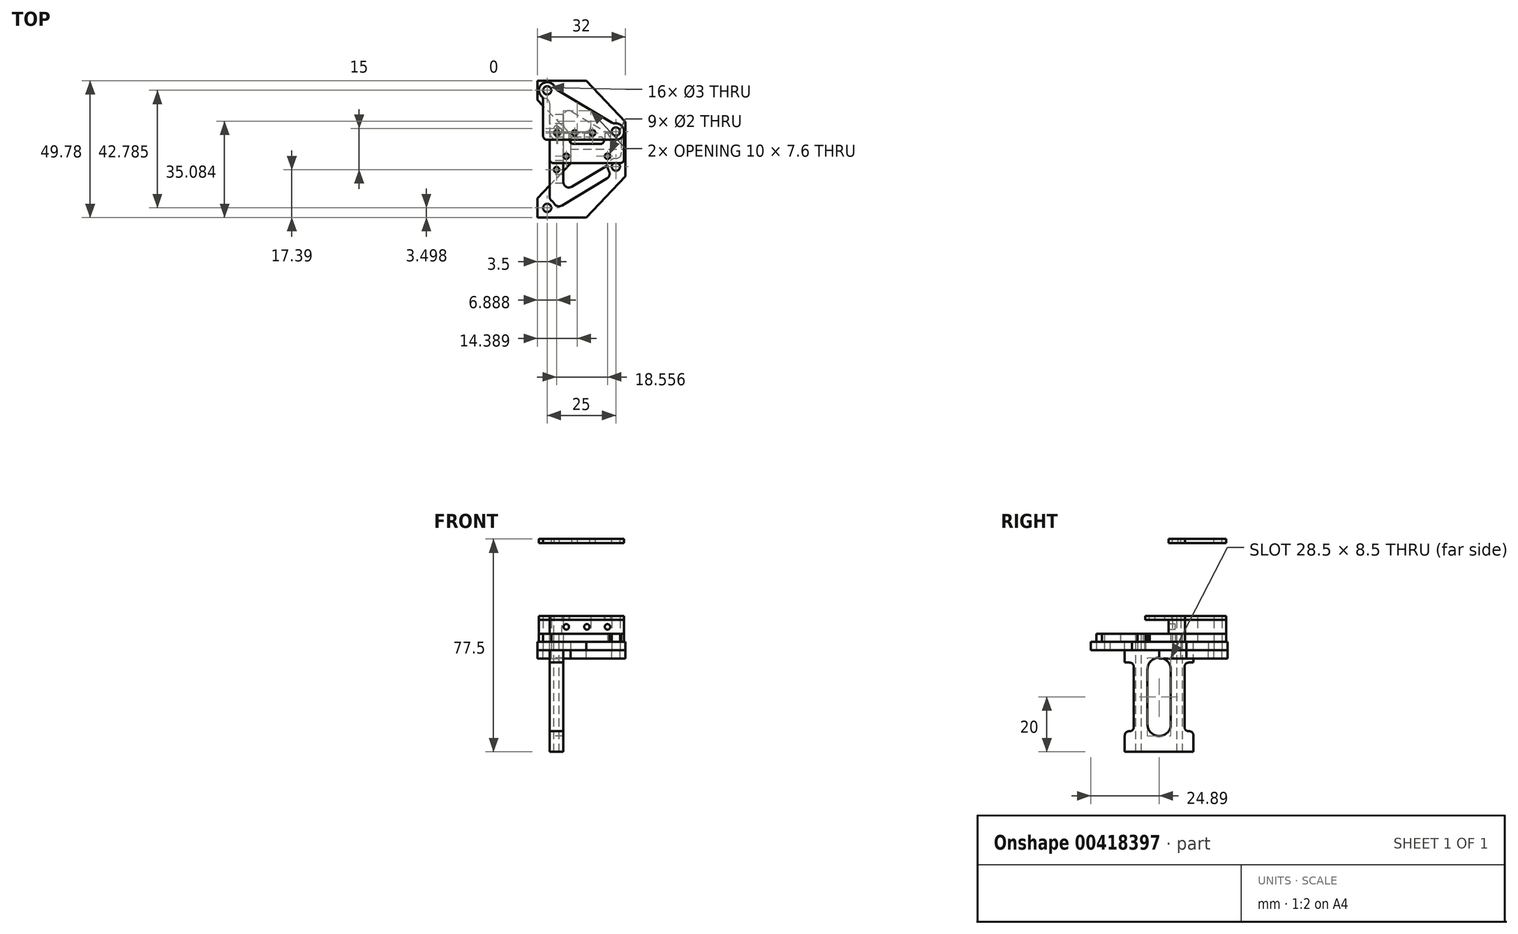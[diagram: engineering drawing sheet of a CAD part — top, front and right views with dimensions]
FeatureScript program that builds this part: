
annotation { "Feature Type Name" : "Feature", "Feature Type Description" : "" }
export const myFeature = defineFeature(function(context is Context, id is Id, definition is map)
    precondition{}
    {
        {
            var Q0;
            Q0=qCreatedBy(makeId("Top.planeOp"),FACE);
            var sketch = newSketch(context, id + "F0", { "sketchPlane" : qUnion([Q0])});
            skCircle(sketch, "E0", {"center": v(0, 21.4) * mm, "radius": 1.5 * mm});
            skCircle(sketch, "E1", {"center": v(25, 6.4) * mm, "radius": 1.5 * mm});
            skCircle(sketch, "E2.MirrorC", {"center": v(0, -21.4) * mm, "radius": 1.5 * mm});
            skCircle(sketch, "E3.MirrorC", {"center": v(25, -6.4) * mm, "radius": 1.5 * mm});
            skLineSegment(sketch, "E4", {"start": v(8.5, 5.26) * mm, "end": v(-3.5, 17.9) * mm});
            skLineSegment(sketch, "E5", {"start": v(-3.5, 17.9) * mm, "end": v(-3.5, 24.9) * mm});
            skLineSegment(sketch, "E6", {"start": v(-3.5, 24.9) * mm, "end": v(14.25, 24.9) * mm});
            skLineSegment(sketch, "E7", {"start": v(14.25, 24.9) * mm, "end": v(28.5, 9.9) * mm});
            skLineSegment(sketch, "E8", {"start": v(28.5, 9.9) * mm, "end": v(28.5, 0) * mm});
            skLineSegment(sketch, "E9.MirrorCS", {"start": v(8.5, -5.26) * mm, "end": v(-3.5, -17.9) * mm});
            skLineSegment(sketch, "E10.MirrorCS", {"start": v(-3.5, -17.9) * mm, "end": v(-3.5, -24.9) * mm});
            skLineSegment(sketch, "E11.MirrorCS", {"start": v(-3.5, -24.9) * mm, "end": v(14.25, -24.9) * mm});
            skLineSegment(sketch, "E12.MirrorCS", {"start": v(14.25, -24.9) * mm, "end": v(28.5, -9.9) * mm});
            skLineSegment(sketch, "E13.MirrorCS", {"start": v(28.5, -9.9) * mm, "end": v(28.5, 0) * mm});
            skLineSegment(sketch, "E14", {"start": v(8.5, 5.26) * mm, "end": v(8.5, -5.26) * mm});
            skPoint(sketch, "E15.orphan", {"position": v(13.5, 0) * mm});
            skLineSegment(sketch, "E16", {"start": v(8.5, 0) * mm, "end": v(28.5, 0) * mm});
            skSolve(sketch);
        }
        {
            var Q0;
            Q0=qSketchRegion(id+"F0",true);
            extrude(context, id + "F1", {"entities" : qUnion([Q0]), "depth" : 3 * mm, "offsetDistance" : 25 * mm});
        }
        {
            var Q0;
            Q0=makeQuery(id+"F0.imprint","IMPRINT",FACE,{"disambiguationData":[TD([[makeQuery(id+"F0.imprint","IMPRINT",EDGE,{"derivedFrom":sQuery(id+"F0.wireOp",EDGE,"E0")}),-1.0]])]});
            extrude(context, id + "F2", {"entities" : qUnion([Q0]), "oppositeDirection" : true, "depth" : 3 * mm, "offsetDistance" : 25 * mm});
        }
        {
            var Q0;
            Q0=makeQuery(id+"F1.opExtrude","CAP_FACE",FACE,{"disambiguationData":[OSD([sQuery(id+"F0.wireOp",EDGE,"E0"),sQuery(id+"F0.wireOp",EDGE,"E1"),sQuery(id+"F0.wireOp",EDGE,"E2.MirrorC"),sQuery(id+"F0.wireOp",EDGE,"E3.MirrorC"),sQuery(id+"F0.wireOp",EDGE,"E4"),sQuery(id+"F0.wireOp",EDGE,"E5"),sQuery(id+"F0.wireOp",EDGE,"E6"),sQuery(id+"F0.wireOp",EDGE,"E7"),sQuery(id+"F0.wireOp",EDGE,"E8"),sQuery(id+"F0.wireOp",EDGE,"E9.MirrorCS"),sQuery(id+"F0.wireOp",EDGE,"E10.MirrorCS"),sQuery(id+"F0.wireOp",EDGE,"E11.MirrorCS"),sQuery(id+"F0.wireOp",EDGE,"E12.MirrorCS"),sQuery(id+"F0.wireOp",EDGE,"E13.MirrorCS"),sQuery(id+"F0.wireOp",EDGE,"E14")])],"isStart":false});
            var sketch = newSketch(context, id + "F3", { "sketchPlane" : qUnion([Q0])});
            skCircle(sketch, "E17.0", {"center": v(0, 21.4) * mm, "radius": 1.5 * mm});
            skCircle(sketch, "E18.0", {"center": v(25, 6.4) * mm, "radius": 1.5 * mm});
            skCircle(sketch, "E19", {"center": v(0, 21.4) * mm, "radius": 3 * mm});
            skCircle(sketch, "E20", {"center": v(25, 6.4) * mm, "radius": 3 * mm});
            skPoint(sketch, "E21", {"position": v(1.5, 21.4) * mm});
            skPoint(sketch, "E22", {"position": v(3, 21.4) * mm});
            skPoint(sketch, "E23", {"position": v(26.5, 6.4) * mm});
            skPoint(sketch, "E24", {"position": v(28, 6.4) * mm});
            skLineSegment(sketch, "E25", {"start": v(0, 21.4) * mm, "end": v(25, 6.4) * mm, "construction": true});
            skCircle(sketch, "E26.0", {"center": v(25, -6.4) * mm, "radius": 1.5 * mm});
            skLineSegment(sketch, "E27", {"start": v(25, 6.4) * mm, "end": v(25, -6.4) * mm, "construction": true});
            skCircle(sketch, "E28.MirrorC", {"center": v(25, -6.4) * mm, "radius": 3 * mm});
            skCircle(sketch, "E29.MirrorC", {"center": v(0, -21.4) * mm, "radius": 3 * mm});
            skLineSegment(sketch, "E30", {"start": v(23, 4.16) * mm, "end": v(23, -4.16) * mm});
            skLineSegment(sketch, "E31.MirrorCS", {"start": v(27, 4.16) * mm, "end": v(27, -4.16) * mm});
            skLineSegment(sketch, "E32", {"start": v(0.89, 18.53) * mm, "end": v(22.05, 5.83) * mm});
            skLineSegment(sketch, "E33.MirrorCS", {"start": v(2.95, 21.96) * mm, "end": v(24.11, 9.26) * mm});
            skLineSegment(sketch, "E34.MirrorCS", {"start": v(0.89, -18.53) * mm, "end": v(22.05, -5.83) * mm});
            skLineSegment(sketch, "E35.MirrorCS", {"start": v(2.95, -21.96) * mm, "end": v(24.11, -9.26) * mm});
            skLineSegment(sketch, "E36", {"start": v(0.89, 18.53) * mm, "end": v(0.89, -18.53) * mm});
            skLineSegment(sketch, "E37", {"start": v(5.89, 15.53) * mm, "end": v(5.89, -15.53) * mm});
            skSolve(sketch);
        }
        {
            var Q0;
            Q0=makeQuery(id+"F3.imprint","IMPRINT",FACE,{"disambiguationData":[TD([[makeQuery(id+"F3.imprint","IMPRINT",EDGE,{"derivedFrom":sQuery(id+"F3.wireOp",EDGE,"E17.0")}),-1.0]])]});
            var Q1;
            Q1=makeQuery(id+"F3.imprint","IMPRINT",FACE,{"disambiguationData":[TD([[makeQuery(id+"F3.imprint","IMPRINT",EDGE,{"derivedFrom":makeQuery(id+"F1.opExtrude","CAP_EDGE",EDGE,{"disambiguationData":[OSD([sQuery(id+"F0.wireOp",EDGE,"E2.MirrorC")])],"isStart":false})}),1.0]])]});
            var Q2;
            {var subQ0=sQuery(id+"F3.wireOp",EDGE,"E30");Q2=makeQuery(id+"F3.imprint","IMPRINT",FACE,{"disambiguationData":[TD([[makeQuery(id+"F3.imprint","IMPRINT",EDGE,{"derivedFrom":subQ0}),1.0]])]});}
            var Q3;
            Q3=makeQuery(id+"F3.imprint","IMPRINT",FACE,{"disambiguationData":[TD([[makeQuery(id+"F3.imprint","IMPRINT",EDGE,{"derivedFrom":sQuery(id+"F3.wireOp",EDGE,"E18.0")}),-1.0]])]});
            var Q4;
            {var subQ6=sQuery(id+"F3.wireOp",EDGE,"E33.MirrorCS");Q4=makeQuery(id+"F3.imprint","IMPRINT",FACE,{"disambiguationData":[TD([[makeQuery(id+"F3.imprint","IMPRINT",EDGE,{"derivedFrom":subQ6}),-1.0]])]});}
            var Q5;
            Q5=makeQuery(id+"F3.imprint","IMPRINT",FACE,{"disambiguationData":[TD([[makeQuery(id+"F3.imprint","IMPRINT",EDGE,{"derivedFrom":sQuery(id+"F3.wireOp",EDGE,"E26.0")}),1.0]])]});
            var Q6;
            {var subQ6=sQuery(id+"F3.wireOp",EDGE,"E35.MirrorCS");Q6=makeQuery(id+"F3.imprint","IMPRINT",FACE,{"disambiguationData":[TD([[makeQuery(id+"F3.imprint","IMPRINT",EDGE,{"derivedFrom":subQ6}),1.0]])]});}
            var Q7;
            {var subQ1=sQuery(id+"F3.wireOp",EDGE,"E32");var subQ3=sQuery(id+"F3.wireOp",EDGE,"E37");var subQ4=makeQuery(id+"F3.imprint","INTERSECT",VERTEX,{"derivedFrom":[subQ1,subQ3]});Q7=makeQuery(id+"F3.imprint","IMPRINT",FACE,{"disambiguationData":[TD([[makeQuery(id+"F3.imprint","IMPRINT",EDGE,{"disambiguationData":[TD([[subQ4,-1.0]])],"derivedFrom":subQ3}),-1.0]])]});}
            var Q8;
            {var subQ1=sQuery(id+"F3.wireOp",EDGE,"E34.MirrorCS");var subQ3=sQuery(id+"F3.wireOp",EDGE,"E37");var subQ4=makeQuery(id+"F3.imprint","INTERSECT",VERTEX,{"derivedFrom":[subQ1,subQ3]});Q8=makeQuery(id+"F3.imprint","IMPRINT",FACE,{"disambiguationData":[TD([[makeQuery(id+"F3.imprint","IMPRINT",EDGE,{"disambiguationData":[TD([[subQ4,1.0]])],"derivedFrom":subQ3}),-1.0]])]});}
            var Q9;
            {var subQ0=sQuery(id+"F3.wireOp",EDGE,"E36");var subQ1=makeQuery(id+"F1.opExtrude","CAP_EDGE",EDGE,{"disambiguationData":[OSD([sQuery(id+"F0.wireOp",EDGE,"E4")])],"isStart":false});var subQ2=makeQuery(id+"F3.imprint","INTERSECT",VERTEX,{"derivedFrom":[subQ1,subQ0]});Q9=makeQuery(id+"F3.imprint","IMPRINT",FACE,{"disambiguationData":[TD([[makeQuery(id+"F3.imprint","IMPRINT",EDGE,{"disambiguationData":[TD([[subQ2,-1.0]])],"derivedFrom":subQ0}),1.0]])]});}
            extrude(context, id + "F4", {"entities" : qUnion([Q0, Q1, Q2, Q3, Q4, Q5, Q6, Q7, Q8, Q9]), "depth" : 3 * mm, "offsetDistance" : 25 * mm});
        }
        {
            var Q0;
            Q0=makeQuery(id+"F4.opExtrude","SWEPT_EDGE",EDGE,{"disambiguationData":[OSD([sQuery(id+"F3.wireOp",EDGE,"E19"),sQuery(id+"F3.wireOp",EDGE,"E32"),sQuery(id+"F3.wireOp",EDGE,"E36")])]});
            var Q1;
            Q1=makeQuery(id+"F4.opExtrude","SWEPT_EDGE",EDGE,{"disambiguationData":[OSD([sQuery(id+"F3.wireOp",EDGE,"E29.MirrorC"),sQuery(id+"F3.wireOp",EDGE,"E34.MirrorCS"),sQuery(id+"F3.wireOp",EDGE,"E36")])]});
            var Q2;
            Q2=makeQuery(id+"F4.opExtrude","SWEPT_EDGE",EDGE,{"disambiguationData":[OSD([sQuery(id+"F3.wireOp",EDGE,"E29.MirrorC"),sQuery(id+"F3.wireOp",EDGE,"E35.MirrorCS")])]});
            var Q3;
            Q3=makeQuery(id+"F4.opExtrude","SWEPT_EDGE",EDGE,{"disambiguationData":[OSD([sQuery(id+"F3.wireOp",EDGE,"E28.MirrorC"),sQuery(id+"F3.wireOp",EDGE,"E35.MirrorCS")])]});
            var Q4;
            Q4=makeQuery(id+"F4.opExtrude","SWEPT_EDGE",EDGE,{"disambiguationData":[OSD([sQuery(id+"F3.wireOp",EDGE,"E20"),sQuery(id+"F3.wireOp",EDGE,"E31.MirrorCS")])]});
            var Q5;
            Q5=makeQuery(id+"F4.opExtrude","SWEPT_EDGE",EDGE,{"disambiguationData":[OSD([sQuery(id+"F3.wireOp",EDGE,"E28.MirrorC"),sQuery(id+"F3.wireOp",EDGE,"E31.MirrorCS")])]});
            var Q6;
            Q6=makeQuery(id+"F4.opExtrude","SWEPT_EDGE",EDGE,{"disambiguationData":[OSD([sQuery(id+"F3.wireOp",EDGE,"E20"),sQuery(id+"F3.wireOp",EDGE,"E33.MirrorCS")])]});
            var Q7;
            Q7=makeQuery(id+"F4.opExtrude","SWEPT_EDGE",EDGE,{"disambiguationData":[OSD([sQuery(id+"F3.wireOp",EDGE,"E34.MirrorCS"),sQuery(id+"F3.wireOp",EDGE,"E37")])]});
            var Q8;
            Q8=makeQuery(id+"F4.opExtrude","SWEPT_EDGE",EDGE,{"disambiguationData":[OSD([sQuery(id+"F3.wireOp",EDGE,"E32"),sQuery(id+"F3.wireOp",EDGE,"E37")])]});
            var Q9;
            Q9=makeQuery(id+"F4.opExtrude","SWEPT_EDGE",EDGE,{"disambiguationData":[OSD([sQuery(id+"F3.wireOp",EDGE,"E19"),sQuery(id+"F3.wireOp",EDGE,"E33.MirrorCS")])]});
            fillet(context, id + "F5", {"entities" : qUnion([Q0, Q1, Q2, Q3, Q4, Q5, Q6, Q7, Q8, Q9]), "radius" : 2 * mm, "tangentPropagation" : true, "allowEdgeOverflow" : false});
        }
        {
            var Q0;
            Q0=makeQuery(id+"F4.opExtrude","CAP_FACE",FACE,{"disambiguationData":[OSD([sQuery(id+"F0.wireOp",EDGE,"E2.MirrorC"),sQuery(id+"F3.wireOp",EDGE,"E17.0"),sQuery(id+"F3.wireOp",EDGE,"E18.0"),sQuery(id+"F3.wireOp",EDGE,"E19"),sQuery(id+"F3.wireOp",EDGE,"E20"),sQuery(id+"F3.wireOp",EDGE,"E26.0"),sQuery(id+"F3.wireOp",EDGE,"E28.MirrorC"),sQuery(id+"F3.wireOp",EDGE,"E29.MirrorC"),sQuery(id+"F3.wireOp",EDGE,"E30"),sQuery(id+"F3.wireOp",EDGE,"E31.MirrorCS"),sQuery(id+"F3.wireOp",EDGE,"E32"),sQuery(id+"F3.wireOp",EDGE,"E33.MirrorCS"),sQuery(id+"F3.wireOp",EDGE,"E34.MirrorCS"),sQuery(id+"F3.wireOp",EDGE,"E35.MirrorCS"),sQuery(id+"F3.wireOp",EDGE,"E36"),sQuery(id+"F3.wireOp",EDGE,"E37")])],"isStart":false});
            var sketch = newSketch(context, id + "F6", { "sketchPlane" : qUnion([Q0])});
            skCircle(sketch, "E38.0", {"center": v(0, 21.4) * mm, "radius": 3 * mm});
            skCircle(sketch, "E39.0", {"center": v(0, 21.4) * mm, "radius": 1.5 * mm});
            skCircle(sketch, "E40.0", {"center": v(25, 6.4) * mm, "radius": 1.5 * mm});
            skCircle(sketch, "E41.0", {"center": v(25, 6.4) * mm, "radius": 3 * mm});
            skArc(sketch, "E42.0", {"start": v(3.6, 21.56) * mm, "mid": v(3.11, 21.98) * mm, "end": v(2.78, 22.52) * mm});
            skLineSegment(sketch, "E43.0", {"start": v(2.95, 21.96) * mm, "end": v(24.11, 9.26) * mm});
            skArc(sketch, "E44.0", {"start": v(24.7, 9.38) * mm, "mid": v(24.05, 9.41) * mm, "end": v(23.46, 9.65) * mm});
            skArc(sketch, "E45.0", {"start": v(-0.67, 18.47) * mm, "mid": v(0.45, 17.76) * mm, "end": v(0.89, 16.52) * mm});
            skLineSegment(sketch, "E46.0", {"start": v(0.89, 18.53) * mm, "end": v(0.89, 3.4) * mm});
            skArc(sketch, "E47.0", {"start": v(5.89, 12) * mm, "mid": v(6.9, 13.74) * mm, "end": v(8.92, 13.7) * mm});
            skLineSegment(sketch, "E48.0", {"start": v(5.89, 15.53) * mm, "end": v(5.89, 3.4) * mm});
            skLineSegment(sketch, "E49.0", {"start": v(0.89, 18.53) * mm, "end": v(14.92, 10.1) * mm});
            skLineSegment(sketch, "E50", {"start": v(25, 3.4) * mm, "end": v(5.89, 3.4) * mm});
            skLineSegment(sketch, "E51", {"start": v(5.89, 6.4) * mm, "end": v(13.9, 6.4) * mm});
            skLineSegment(sketch, "E52", {"start": v(5.89, 3.4) * mm, "end": v(0.89, 3.4) * mm});
            skPoint(sketch, "E53.orphan", {"position": v(0.89, -18.53) * mm});
            skPoint(sketch, "E54.orphan", {"position": v(5.89, -15.53) * mm});
            skPoint(sketch, "E55.newPointA", {"position": v(22.05, 5.83) * mm});
            skArc(sketch, "E55.filletArc", {"start": v(13.9, 6.4) * mm, "mid": v(15.82, 7.86) * mm, "end": v(14.92, 10.1) * mm});
            skSolve(sketch);
        }
        {
            var Q0;
            Q0=qSketchRegion(id+"F6",true);
            var Q1;
            {var subQ0=sQuery(id+"F6.wireOp",EDGE,"E47.0");Q1=makeQuery(id+"F6.imprint","IMPRINT",FACE,{"disambiguationData":[TD([[makeQuery(id+"F6.imprint","IMPRINT",EDGE,{"derivedFrom":subQ0}),1.0]])]});}
            extrude(context, id + "F7", {"entities" : qUnion([Q0, Q1]), "depth" : 5 * mm, "offsetDistance" : 25 * mm});
        }
        {
            var Q0;
            Q0=makeQuery(id+"F7.opExtrude","SWEPT_EDGE",EDGE,{"disambiguationData":[OSD([sQuery(id+"F6.wireOp",EDGE,"E48.0"),sQuery(id+"F6.wireOp",EDGE,"E51")])]});
            var Q1;
            Q1=makeQuery(id+"F7.opExtrude","SWEPT_EDGE",EDGE,{"disambiguationData":[OSD([sQuery(id+"F3.wireOp",EDGE,"E36"),sQuery(id+"F6.wireOp",EDGE,"E46.0"),sQuery(id+"F6.wireOp",EDGE,"E52")])]});
            fillet(context, id + "F8", {"entities" : qUnion([Q0, Q1]), "radius" : 3 * mm, "tangentPropagation" : true, "allowEdgeOverflow" : false});
        }
        {
            var Q0;
            Q0=makeQuery(id+"F4.opExtrude","CAP_FACE",FACE,{"disambiguationData":[OSD([sQuery(id+"F0.wireOp",EDGE,"E2.MirrorC"),sQuery(id+"F3.wireOp",EDGE,"E17.0"),sQuery(id+"F3.wireOp",EDGE,"E18.0"),sQuery(id+"F3.wireOp",EDGE,"E19"),sQuery(id+"F3.wireOp",EDGE,"E20"),sQuery(id+"F3.wireOp",EDGE,"E26.0"),sQuery(id+"F3.wireOp",EDGE,"E28.MirrorC"),sQuery(id+"F3.wireOp",EDGE,"E29.MirrorC"),sQuery(id+"F3.wireOp",EDGE,"E30"),sQuery(id+"F3.wireOp",EDGE,"E31.MirrorCS"),sQuery(id+"F3.wireOp",EDGE,"E32"),sQuery(id+"F3.wireOp",EDGE,"E33.MirrorCS"),sQuery(id+"F3.wireOp",EDGE,"E34.MirrorCS"),sQuery(id+"F3.wireOp",EDGE,"E35.MirrorCS"),sQuery(id+"F3.wireOp",EDGE,"E36"),sQuery(id+"F3.wireOp",EDGE,"E37")])],"isStart":false});
            var sketch = newSketch(context, id + "F9", { "sketchPlane" : qUnion([Q0])});
            skLineSegment(sketch, "E56", {"start": v(5.89, 0) * mm, "end": v(0.89, 0) * mm, "construction": true});
            skLineSegment(sketch, "E57", {"start": v(3.39, 0) * mm, "end": v(3.39, 16.52) * mm, "construction": true});
            skCircle(sketch, "E58", {"center": v(3.39, 7.5) * mm, "radius": 1 * mm});
            skCircle(sketch, "E59.MirrorC", {"center": v(3.39, -7.5) * mm, "radius": 1 * mm});
            skSolve(sketch);
        }
        {
            var Q0;
            Q0=qSketchRegion(id+"F9",true);
            extrude(context, id + "F10", {"entities" : qUnion([Q0]), "operationType" : NewBodyOperationType.REMOVE, "endBound" : BoundingType.UP_TO_NEXT, "oppositeDirection" : true, "depth" : 25 * mm, "offsetDistance" : 25 * mm});
        }
        {
            var Q0;
            Q0=makeQuery(id+"F7.opExtrude","CAP_FACE",FACE,{"disambiguationData":[OSD([sQuery(id+"F6.wireOp",EDGE,"E38.0"),sQuery(id+"F6.wireOp",EDGE,"E39.0"),sQuery(id+"F6.wireOp",EDGE,"E40.0"),sQuery(id+"F6.wireOp",EDGE,"E41.0"),sQuery(id+"F6.wireOp",EDGE,"E42.0"),sQuery(id+"F6.wireOp",EDGE,"E43.0"),sQuery(id+"F6.wireOp",EDGE,"E44.0"),sQuery(id+"F6.wireOp",EDGE,"E45.0"),sQuery(id+"F6.wireOp",EDGE,"E46.0"),sQuery(id+"F6.wireOp",EDGE,"E47.0"),sQuery(id+"F6.wireOp",EDGE,"E48.0"),sQuery(id+"F6.wireOp",EDGE,"E49.0"),sQuery(id+"F6.wireOp",EDGE,"E50"),sQuery(id+"F6.wireOp",EDGE,"E51"),sQuery(id+"F6.wireOp",EDGE,"E52"),sQuery(id+"F6.wireOp",EDGE,"E55.filletArc")])],"isStart":false});
            var sketch = newSketch(context, id + "F11", { "sketchPlane" : qUnion([Q0])});
            skArc(sketch, "E60.0", {"start": v(0.89, 6.4) * mm, "mid": v(1.77, 4.27) * mm, "end": v(3.89, 3.4) * mm, "construction": true});
            skCircle(sketch, "E61", {"center": v(3.89, 6.4) * mm, "radius": 1.5 * mm});
            skSolve(sketch);
        }
        {
            var Q0;
            Q0=qSketchRegion(id+"F11",true);
            extrude(context, id + "F12", {"entities" : qUnion([Q0]), "operationType" : NewBodyOperationType.REMOVE, "endBound" : BoundingType.UP_TO_NEXT, "oppositeDirection" : true, "depth" : 25 * mm, "offsetDistance" : 25 * mm});
        }
        {
            var Q0;
            Q0=makeQuery(id+"F7.opExtrude","SWEPT_FACE",FACE,{"disambiguationData":[OSD([sQuery(id+"F6.wireOp",EDGE,"E50"),sQuery(id+"F6.wireOp",EDGE,"E52")])]});
            var sketch = newSketch(context, id + "F13", { "sketchPlane" : qUnion([Q0])});
            skLineSegment(sketch, "E62", {"start": v(3.89, 8.5) * mm, "end": v(25, 8.5) * mm, "construction": true});
            skLineSegment(sketch, "E63", {"start": v(14.44, 11) * mm, "end": v(14.44, 6) * mm, "construction": true});
            skCircle(sketch, "E64", {"center": v(6.94, 8.5) * mm, "radius": 1 * mm});
            skCircle(sketch, "E65", {"center": v(14.44, 8.5) * mm, "radius": 1 * mm});
            skCircle(sketch, "E66.MirrorC", {"center": v(21.94, 8.5) * mm, "radius": 1 * mm});
            skSolve(sketch);
        }
        {
            var Q0;
            Q0 = qSketchRegion(id + "F13", true);
            extrude(context, id + "F14", {"entities" : qUnion([Q0]), "operationType" : NewBodyOperationType.REMOVE, "oppositeDirection" : true, "depth" : 2.5 * mm, "offsetDistance" : 25 * mm});
        }
        {
            var Q0;
            Q0=makeQuery(id+"F4.opExtrude","CAP_FACE",FACE,{"disambiguationData":[OSD([sQuery(id+"F0.wireOp",EDGE,"E2.MirrorC"),sQuery(id+"F3.wireOp",EDGE,"E17.0"),sQuery(id+"F3.wireOp",EDGE,"E18.0"),sQuery(id+"F3.wireOp",EDGE,"E19"),sQuery(id+"F3.wireOp",EDGE,"E20"),sQuery(id+"F3.wireOp",EDGE,"E26.0"),sQuery(id+"F3.wireOp",EDGE,"E28.MirrorC"),sQuery(id+"F3.wireOp",EDGE,"E29.MirrorC"),sQuery(id+"F3.wireOp",EDGE,"E30"),sQuery(id+"F3.wireOp",EDGE,"E31.MirrorCS"),sQuery(id+"F3.wireOp",EDGE,"E32"),sQuery(id+"F3.wireOp",EDGE,"E33.MirrorCS"),sQuery(id+"F3.wireOp",EDGE,"E34.MirrorCS"),sQuery(id+"F3.wireOp",EDGE,"E35.MirrorCS"),sQuery(id+"F3.wireOp",EDGE,"E36"),sQuery(id+"F3.wireOp",EDGE,"E37")])],"isStart":true});
            var sketch = newSketch(context, id + "F15", { "sketchPlane" : qUnion([Q0])});
            skCircle(sketch, "E67.0", {"center": v(3.39, 7.5) * mm, "radius": 1 * mm});
            skCircle(sketch, "E68.0", {"center": v(3.39, -7.5) * mm, "radius": 1 * mm});
            skLineSegment(sketch, "E69", {"start": v(3.39, 7.5) * mm, "end": v(3.39, -7.5) * mm, "construction": true});
            skLineSegment(sketch, "E70.bottom", {"start": v(0.89, 12.5) * mm, "end": v(5.89, 12.5) * mm});
            skLineSegment(sketch, "E70.top", {"start": v(0.89, -12.5) * mm, "end": v(5.89, -12.5) * mm});
            skLineSegment(sketch, "E70.left", {"start": v(0.89, 12.5) * mm, "end": v(0.89, -12.5) * mm});
            skLineSegment(sketch, "E70.right", {"start": v(5.89, 12.5) * mm, "end": v(5.89, -12.5) * mm});
            skPoint(sketch, "E70.middle", {"position": v(3.39, 0) * mm});
            skSolve(sketch);
        }
        {
            var Q0;
            Q0 = qSketchRegion(id + "F15", true);
            extrude(context, id + "F16", {"entities" : qUnion([Q0]), "depth" : 40 * mm, "offsetDistance" : 25 * mm});
        }
        {
            var Q0;
            Q0=makeQuery(id+"F16.opExtrude","SWEPT_FACE",FACE,{"disambiguationData":[OSD([sQuery(id+"F15.wireOp",EDGE,"E70.left")])]});
            var sketch = newSketch(context, id + "F17", { "sketchPlane" : qUnion([Q0])});
            skArc(sketch, "E71", {"start": v(4.25, -7) * mm, "mid": v(0, -2.75) * mm, "end": v(-4.25, -7) * mm});
            skLineSegment(sketch, "E72", {"start": v(0, 3) * mm, "end": v(0, -37) * mm, "construction": true});
            skLineSegment(sketch, "E73", {"start": v(12.5, -17) * mm, "end": v(-12.5, -17) * mm, "construction": true});
            skArc(sketch, "E74.MirrorC", {"start": v(4.25, -27) * mm, "mid": v(0, -31.25) * mm, "end": v(-4.25, -27) * mm});
            skLineSegment(sketch, "E75", {"start": v(4.25, -7) * mm, "end": v(4.25, -27) * mm});
            skLineSegment(sketch, "E76.MirrorCS", {"start": v(-4.25, -7) * mm, "end": v(-4.25, -27) * mm});
            skLineSegment(sketch, "E77.bottom", {"start": v(12.5, -4.5) * mm, "end": v(10.75, -4.5) * mm});
            skLineSegment(sketch, "E77.top", {"start": v(12.5, -29.5) * mm, "end": v(10.75, -29.5) * mm});
            skLineSegment(sketch, "E77.left", {"start": v(12.5, -4.5) * mm, "end": v(12.5, -29.5) * mm});
            skLineSegment(sketch, "E77.right", {"start": v(9.25, -6) * mm, "end": v(9.25, -28) * mm});
            skPoint(sketch, "E78", {"position": v(9.25, -17) * mm});
            skPoint(sketch, "E79.visualSharp", {"position": v(9.25, -4.5) * mm});
            skArc(sketch, "E79.filletArc", {"start": v(10.75, -4.5) * mm, "mid": v(9.69, -4.94) * mm, "end": v(9.25, -6) * mm});
            skPoint(sketch, "E80.visualSharp", {"position": v(9.25, -29.5) * mm});
            skArc(sketch, "E80.filletArc", {"start": v(9.25, -28) * mm, "mid": v(9.69, -29.06) * mm, "end": v(10.75, -29.5) * mm});
            skLineSegment(sketch, "E81.MirrorCS", {"start": v(-12.5, -29.5) * mm, "end": v(-10.75, -29.5) * mm});
            skLineSegment(sketch, "E82.MirrorCS", {"start": v(-12.5, -4.5) * mm, "end": v(-10.75, -4.5) * mm});
            skArc(sketch, "E83.MirrorCS", {"start": v(-9.25, -28) * mm, "mid": v(-9.69, -29.06) * mm, "end": v(-10.75, -29.5) * mm});
            skArc(sketch, "E84.MirrorCS", {"start": v(-10.75, -4.5) * mm, "mid": v(-9.69, -4.94) * mm, "end": v(-9.25, -6) * mm});
            skLineSegment(sketch, "E85.MirrorCS", {"start": v(-9.25, -6) * mm, "end": v(-9.25, -28) * mm});
            skPoint(sketch, "E86.MirrorP", {"position": v(-9.25, -29.5) * mm});
            skLineSegment(sketch, "E87.MirrorCS", {"start": v(-12.5, -4.5) * mm, "end": v(-12.5, -29.5) * mm});
            skPoint(sketch, "E88.MirrorP", {"position": v(-9.25, -4.5) * mm});
            skPoint(sketch, "E89.MirrorP", {"position": v(-9.25, -17) * mm});
            skSolve(sketch);
        }
        {
            var Q0;
            Q0 = qSketchRegion(id + "F17", true);
            extrude(context, id + "F18", {"entities" : qUnion([Q0]), "operationType" : NewBodyOperationType.REMOVE, "endBound" : BoundingType.UP_TO_NEXT, "oppositeDirection" : true, "depth" : 25 * mm, "offsetDistance" : 25 * mm});
        }
        {
            var Q0;
            Q0=makeQuery(id+"F18.boolean.opBoolean","COPY",EDGE,{"derivedFrom":makeQuery(id+"F18.opExtrude","SWEPT_EDGE",EDGE,{"disambiguationData":[OSD([sQuery(id+"F3.wireOp",EDGE,"E36"),sQuery(id+"F15.wireOp",EDGE,"E70.bottom"),sQuery(id+"F15.wireOp",EDGE,"E70.left"),sQuery(id+"F17.wireOp",EDGE,"E77.bottom"),sQuery(id+"F17.wireOp",EDGE,"E77.left")])]})});
            var Q1;
            Q1=makeQuery(id+"F18.boolean.opBoolean","COPY",EDGE,{"derivedFrom":makeQuery(id+"F18.opExtrude","SWEPT_EDGE",EDGE,{"disambiguationData":[OSD([sQuery(id+"F3.wireOp",EDGE,"E36"),sQuery(id+"F15.wireOp",EDGE,"E70.top"),sQuery(id+"F15.wireOp",EDGE,"E70.left"),sQuery(id+"F17.wireOp",EDGE,"E82.MirrorCS"),sQuery(id+"F17.wireOp",EDGE,"E87.MirrorCS")])]})});
            var Q2;
            Q2=makeQuery(id+"F18.boolean.opBoolean","COPY",EDGE,{"derivedFrom":makeQuery(id+"F18.opExtrude","SWEPT_EDGE",EDGE,{"disambiguationData":[OSD([sQuery(id+"F3.wireOp",EDGE,"E36"),sQuery(id+"F15.wireOp",EDGE,"E70.bottom"),sQuery(id+"F15.wireOp",EDGE,"E70.left"),sQuery(id+"F17.wireOp",EDGE,"E77.top"),sQuery(id+"F17.wireOp",EDGE,"E77.left")])]})});
            var Q3;
            Q3=makeQuery(id+"F18.boolean.opBoolean","COPY",EDGE,{"derivedFrom":makeQuery(id+"F18.opExtrude","SWEPT_EDGE",EDGE,{"disambiguationData":[OSD([sQuery(id+"F3.wireOp",EDGE,"E36"),sQuery(id+"F15.wireOp",EDGE,"E70.top"),sQuery(id+"F15.wireOp",EDGE,"E70.left"),sQuery(id+"F17.wireOp",EDGE,"E81.MirrorCS"),sQuery(id+"F17.wireOp",EDGE,"E87.MirrorCS")])]})});
            fillet(context, id + "F19", {"entities" : qUnion([Q0, Q1, Q2, Q3]), "radius" : 1.5 * mm, "tangentPropagation" : true, "allowEdgeOverflow" : false});
        }
        {
            var Q0;
            Q0=makeQuery(id+"F7.opExtrude","CAP_FACE",FACE,{"disambiguationData":[OSD([sQuery(id+"F6.wireOp",EDGE,"E38.0"),sQuery(id+"F6.wireOp",EDGE,"E39.0"),sQuery(id+"F6.wireOp",EDGE,"E40.0"),sQuery(id+"F6.wireOp",EDGE,"E41.0"),sQuery(id+"F6.wireOp",EDGE,"E42.0"),sQuery(id+"F6.wireOp",EDGE,"E43.0"),sQuery(id+"F6.wireOp",EDGE,"E44.0"),sQuery(id+"F6.wireOp",EDGE,"E45.0"),sQuery(id+"F6.wireOp",EDGE,"E46.0"),sQuery(id+"F6.wireOp",EDGE,"E47.0"),sQuery(id+"F6.wireOp",EDGE,"E48.0"),sQuery(id+"F6.wireOp",EDGE,"E49.0"),sQuery(id+"F6.wireOp",EDGE,"E50"),sQuery(id+"F6.wireOp",EDGE,"E51"),sQuery(id+"F6.wireOp",EDGE,"E52"),sQuery(id+"F6.wireOp",EDGE,"E55.filletArc")])],"isStart":false});
            var sketch = newSketch(context, id + "F20", { "sketchPlane" : qUnion([Q0])});
            skLineSegment(sketch, "E90.0.0", {"start": v(0.89, 16.52) * mm, "end": v(0.89, 6.4) * mm});
            skArc(sketch, "E90.0.3", {"start": v(28, 6.4) * mm, "mid": v(27, 8.62) * mm, "end": v(24.7, 9.38) * mm});
            skArc(sketch, "E90.0.4", {"start": v(24.7, 9.38) * mm, "mid": v(24.05, 9.41) * mm, "end": v(23.46, 9.65) * mm});
            skLineSegment(sketch, "E90.0.5", {"start": v(23.46, 9.65) * mm, "end": v(3.6, 21.56) * mm});
            skArc(sketch, "E90.0.6", {"start": v(3.6, 21.56) * mm, "mid": v(3.11, 21.98) * mm, "end": v(2.78, 22.52) * mm});
            skArc(sketch, "E90.0.7", {"start": v(2.78, 22.52) * mm, "mid": v(-2.29, 23.33) * mm, "end": v(-0.67, 18.47) * mm});
            skArc(sketch, "E90.0.8", {"start": v(-0.67, 18.47) * mm, "mid": v(0.45, 17.76) * mm, "end": v(0.89, 16.52) * mm});
            skArc(sketch, "E91.0", {"start": v(5.89, 12) * mm, "mid": v(6.9, 13.74) * mm, "end": v(8.92, 13.7) * mm});
            skLineSegment(sketch, "E92.0", {"start": v(8.92, 13.7) * mm, "end": v(14.92, 10.1) * mm});
            skLineSegment(sketch, "E93.0", {"start": v(5.89, 12) * mm, "end": v(5.89, 9.4) * mm});
            skArc(sketch, "E94.0", {"start": v(8.89, 6.4) * mm, "mid": v(6.77, 7.27) * mm, "end": v(5.89, 9.4) * mm});
            skLineSegment(sketch, "E95.0", {"start": v(8.89, 6.4) * mm, "end": v(13.9, 6.4) * mm});
            skArc(sketch, "E96.0", {"start": v(13.9, 6.4) * mm, "mid": v(15.82, 7.86) * mm, "end": v(14.92, 10.1) * mm});
            skCircle(sketch, "E97.0", {"center": v(25, 6.4) * mm, "radius": 1.5 * mm});
            skCircle(sketch, "E98.0", {"center": v(3.89, 6.4) * mm, "radius": 1.5 * mm});
            skCircle(sketch, "E99.0", {"center": v(0, 21.4) * mm, "radius": 1.5 * mm});
            skPoint(sketch, "E100", {"position": v(28, 6.4) * mm});
            skPoint(sketch, "E101.orphan", {"position": v(25, 3.4) * mm});
            skLineSegment(sketch, "E102", {"start": v(0.89, 6.4) * mm, "end": v(0.89, -3.6) * mm});
            skLineSegment(sketch, "E103", {"start": v(2.39, -5.1) * mm, "end": v(26.5, -5.1) * mm});
            skLineSegment(sketch, "E104", {"start": v(28, -3.6) * mm, "end": v(28, 6.4) * mm});
            skLineSegment(sketch, "E105", {"start": v(0.89, 3.14) * mm, "end": v(28, 3.14) * mm, "construction": true});
            skLineSegment(sketch, "E106", {"start": v(0.89, 3.4) * mm, "end": v(28, 3.4) * mm, "construction": true});
            skPoint(sketch, "E107.visualSharp", {"position": v(0.89, -5.1) * mm});
            skArc(sketch, "E107.filletArc", {"start": v(0.89, -3.6) * mm, "mid": v(1.33, -4.67) * mm, "end": v(2.39, -5.1) * mm});
            skPoint(sketch, "E108.visualSharp", {"position": v(28, -5.1) * mm});
            skArc(sketch, "E108.filletArc", {"start": v(26.5, -5.1) * mm, "mid": v(27.56, -4.67) * mm, "end": v(28, -3.6) * mm});
            skPoint(sketch, "E109", {"position": v(14.44, -5.1) * mm});
            skCircle(sketch, "E110", {"center": v(6.94, -2.6) * mm, "radius": 1 * mm});
            skCircle(sketch, "E111", {"center": v(21.94, -2.6) * mm, "radius": 1 * mm});
            skCircle(sketch, "E112", {"center": v(14.44, 3.14) * mm, "radius": 1.25 * mm});
            skCircle(sketch, "E113", {"center": v(9.44, 3.14) * mm, "radius": 1.25 * mm});
            skCircle(sketch, "E114", {"center": v(19.44, 3.14) * mm, "radius": 1.25 * mm});
            skLineSegment(sketch, "E115", {"start": v(9.44, 4.4) * mm, "end": v(14.44, 4.4) * mm});
            skLineSegment(sketch, "E116", {"start": v(14.44, 4.4) * mm, "end": v(19.44, 4.4) * mm});
            skLineSegment(sketch, "E117.MirrorCS", {"start": v(9.44, 1.9) * mm, "end": v(14.44, 1.9) * mm});
            skLineSegment(sketch, "E118.MirrorCS", {"start": v(14.44, 1.9) * mm, "end": v(19.44, 1.9) * mm});
            skSolve(sketch);
        }
        {
            var Q0;
            Q0 = qSketchRegion(id + "F20", true);
            extrude(context, id + "F21", {"entities" : qUnion([Q0]), "depth" : 1.5 * mm, "offsetDistance" : 25 * mm});
        }
        {
            var Q0;
            Q0=qCreatedBy(makeId("Top.planeOp"),FACE);
            cPlane(context, id + "F22", {"entities" : qUnion([Q0]), "cplaneType" : CPlaneType.OFFSET, "offset" : 25 * mm, "width" : 150 * mm, "height" : 150 * mm});
        }
        {
            var Q0;
            Q0=makeQuery(id+"F7.opExtrude","SWEPT_BODY",BODY,{"disambiguationData":[OSD([sQuery(id+"F6.wireOp",EDGE,"E38.0"),sQuery(id+"F6.wireOp",EDGE,"E39.0"),sQuery(id+"F6.wireOp",EDGE,"E40.0"),sQuery(id+"F6.wireOp",EDGE,"E41.0"),sQuery(id+"F6.wireOp",EDGE,"E42.0"),sQuery(id+"F6.wireOp",EDGE,"E43.0"),sQuery(id+"F6.wireOp",EDGE,"E44.0"),sQuery(id+"F6.wireOp",EDGE,"E45.0"),sQuery(id+"F6.wireOp",EDGE,"E46.0"),sQuery(id+"F6.wireOp",EDGE,"E47.0"),sQuery(id+"F6.wireOp",EDGE,"E48.0"),sQuery(id+"F6.wireOp",EDGE,"E49.0"),sQuery(id+"F6.wireOp",EDGE,"E50"),sQuery(id+"F6.wireOp",EDGE,"E51"),sQuery(id+"F6.wireOp",EDGE,"E52"),sQuery(id+"F6.wireOp",EDGE,"E55.filletArc")])]});
            var Q1;
            Q1=qCreatedBy(id+"F22.planeOp",FACE);
            mirror(context, id + "F23", {"entities" : qUnion([Q0]), "mirrorPlane" : qUnion([Q1])});
        }
        {
            var Q0;
            Q0=makeQuery(id+"F23.opPattern","COPY",FACE,{"derivedFrom":makeQuery(id+"F7.opExtrude","CAP_FACE",FACE,{"disambiguationData":[OSD([sQuery(id+"F6.wireOp",EDGE,"E38.0"),sQuery(id+"F6.wireOp",EDGE,"E39.0"),sQuery(id+"F6.wireOp",EDGE,"E40.0"),sQuery(id+"F6.wireOp",EDGE,"E41.0"),sQuery(id+"F6.wireOp",EDGE,"E42.0"),sQuery(id+"F6.wireOp",EDGE,"E43.0"),sQuery(id+"F6.wireOp",EDGE,"E44.0"),sQuery(id+"F6.wireOp",EDGE,"E45.0"),sQuery(id+"F6.wireOp",EDGE,"E46.0"),sQuery(id+"F6.wireOp",EDGE,"E47.0"),sQuery(id+"F6.wireOp",EDGE,"E48.0"),sQuery(id+"F6.wireOp",EDGE,"E49.0"),sQuery(id+"F6.wireOp",EDGE,"E50"),sQuery(id+"F6.wireOp",EDGE,"E51"),sQuery(id+"F6.wireOp",EDGE,"E52"),sQuery(id+"F6.wireOp",EDGE,"E55.filletArc")])],"isStart":true}),"instanceName":"1"});
            var sketch = newSketch(context, id + "F24", { "sketchPlane" : qUnion([Q0])});
            skCircle(sketch, "E119.0", {"center": v(3.89, 6.4) * mm, "radius": 1.5 * mm});
            skArc(sketch, "E120.0", {"start": v(5.89, 12) * mm, "mid": v(6.9, 13.74) * mm, "end": v(8.92, 13.7) * mm});
            skLineSegment(sketch, "E121.0", {"start": v(5.89, 12) * mm, "end": v(5.89, 9.4) * mm});
            skArc(sketch, "E122.0", {"start": v(5.89, 9.4) * mm, "mid": v(6.77, 7.27) * mm, "end": v(8.89, 6.4) * mm});
            skLineSegment(sketch, "E123.0", {"start": v(8.89, 6.4) * mm, "end": v(13.9, 6.4) * mm});
            skLineSegment(sketch, "E124.0", {"start": v(8.92, 13.7) * mm, "end": v(14.92, 10.1) * mm});
            skArc(sketch, "E125.0", {"start": v(13.9, 6.4) * mm, "mid": v(15.82, 7.86) * mm, "end": v(14.92, 10.1) * mm});
            skLineSegment(sketch, "E126", {"start": v(0.89, 6.4) * mm, "end": v(0.89, 4.4) * mm});
            skLineSegment(sketch, "E127", {"start": v(1.89, 3.4) * mm, "end": v(3.89, 3.4) * mm});
            skArc(sketch, "E128.0", {"start": v(3.89, 3.4) * mm, "mid": v(1.77, 4.27) * mm, "end": v(0.89, 6.4) * mm});
            skPoint(sketch, "E129.visualSharp", {"position": v(0.89, 3.4) * mm});
            skArc(sketch, "E129.filletArc", {"start": v(0.89, 4.4) * mm, "mid": v(1.18, 3.69) * mm, "end": v(1.89, 3.4) * mm});
            skArc(sketch, "E130.0", {"start": v(-0.67, 18.47) * mm, "mid": v(0.45, 17.76) * mm, "end": v(0.89, 16.52) * mm});
            skLineSegment(sketch, "E131.0", {"start": v(0.89, 16.52) * mm, "end": v(0.89, 6.4) * mm});
            skArc(sketch, "E132.0", {"start": v(2.78, 22.52) * mm, "mid": v(-1.73, 23.84) * mm, "end": v(-2, 19.16) * mm});
            skLineSegment(sketch, "E133", {"start": v(-1.5, 18.04) * mm, "end": v(-1.5, 4.9) * mm});
            skLineSegment(sketch, "E134", {"start": v(0, 3.4) * mm, "end": v(1.89, 3.4) * mm});
            skPoint(sketch, "E135.newPointB", {"position": v(-1.5, 18.8) * mm});
            skArc(sketch, "E135.filletArc", {"start": v(-1.5, 18.04) * mm, "mid": v(-1.63, 18.65) * mm, "end": v(-2, 19.16) * mm});
            skArc(sketch, "E136.0", {"start": v(-2, 19.16) * mm, "mid": v(-1.38, 18.73) * mm, "end": v(-0.67, 18.47) * mm});
            skPoint(sketch, "E137.visualSharp", {"position": v(-1.5, 3.4) * mm});
            skArc(sketch, "E137.filletArc", {"start": v(-1.5, 4.9) * mm, "mid": v(-1.06, 3.83) * mm, "end": v(0, 3.4) * mm});
            skSolve(sketch);
        }
        {
            var Q0;
            Q0 = qSketchRegion(id + "F24", true);
            var Q1;
            Q1=makeQuery(id+"F23.opPattern","COPY",FACE,{"derivedFrom":makeQuery(id+"F7.opExtrude","CAP_FACE",FACE,{"disambiguationData":[OSD([sQuery(id+"F6.wireOp",EDGE,"E38.0"),sQuery(id+"F6.wireOp",EDGE,"E39.0"),sQuery(id+"F6.wireOp",EDGE,"E40.0"),sQuery(id+"F6.wireOp",EDGE,"E41.0"),sQuery(id+"F6.wireOp",EDGE,"E42.0"),sQuery(id+"F6.wireOp",EDGE,"E43.0"),sQuery(id+"F6.wireOp",EDGE,"E44.0"),sQuery(id+"F6.wireOp",EDGE,"E45.0"),sQuery(id+"F6.wireOp",EDGE,"E46.0"),sQuery(id+"F6.wireOp",EDGE,"E47.0"),sQuery(id+"F6.wireOp",EDGE,"E48.0"),sQuery(id+"F6.wireOp",EDGE,"E49.0"),sQuery(id+"F6.wireOp",EDGE,"E50"),sQuery(id+"F6.wireOp",EDGE,"E51"),sQuery(id+"F6.wireOp",EDGE,"E52"),sQuery(id+"F6.wireOp",EDGE,"E55.filletArc")])],"isStart":false}),"instanceName":"1"});
            extrude(context, id + "F25", {"entities" : qUnion([Q0]), "operationType" : NewBodyOperationType.ADD, "endBound" : BoundingType.UP_TO_SURFACE, "oppositeDirection" : true, "depth" : 25 * mm, "endBoundEntityFace" : qUnion([Q1]), "offsetDistance" : 25 * mm});
        }
        {
            var Q0;
            Q0=makeQuery(id+"F25.boolean.opBoolean","MERGE",FACE,{"derivedFrom":[makeQuery(id+"F23.opPattern","COPY",FACE,{"derivedFrom":makeQuery(id+"F7.opExtrude","CAP_FACE",FACE,{"disambiguationData":[OSD([sQuery(id+"F6.wireOp",EDGE,"E38.0"),sQuery(id+"F6.wireOp",EDGE,"E39.0"),sQuery(id+"F6.wireOp",EDGE,"E40.0"),sQuery(id+"F6.wireOp",EDGE,"E41.0"),sQuery(id+"F6.wireOp",EDGE,"E42.0"),sQuery(id+"F6.wireOp",EDGE,"E43.0"),sQuery(id+"F6.wireOp",EDGE,"E44.0"),sQuery(id+"F6.wireOp",EDGE,"E45.0"),sQuery(id+"F6.wireOp",EDGE,"E46.0"),sQuery(id+"F6.wireOp",EDGE,"E47.0"),sQuery(id+"F6.wireOp",EDGE,"E48.0"),sQuery(id+"F6.wireOp",EDGE,"E49.0"),sQuery(id+"F6.wireOp",EDGE,"E50"),sQuery(id+"F6.wireOp",EDGE,"E51"),sQuery(id+"F6.wireOp",EDGE,"E52"),sQuery(id+"F6.wireOp",EDGE,"E55.filletArc")])],"isStart":true}),"instanceName":"1"}),makeQuery(id+"F25.opExtrude","CAP_FACE",FACE,{"disambiguationData":[OSD([sQuery(id+"F24.wireOp",EDGE,"E119.0")])],"isStart":true}),makeQuery(id+"F25.opExtrude","CAP_FACE",FACE,{"disambiguationData":[OSD([sQuery(id+"F24.wireOp",EDGE,"E120.0"),sQuery(id+"F24.wireOp",EDGE,"E121.0"),sQuery(id+"F24.wireOp",EDGE,"E122.0"),sQuery(id+"F24.wireOp",EDGE,"E123.0"),sQuery(id+"F24.wireOp",EDGE,"E124.0"),sQuery(id+"F24.wireOp",EDGE,"E125.0")])],"isStart":true}),makeQuery(id+"F25.opExtrude","CAP_FACE",FACE,{"disambiguationData":[OSD([sQuery(id+"F24.wireOp",EDGE,"E127"),sQuery(id+"F24.wireOp",EDGE,"E128.0"),sQuery(id+"F24.wireOp",EDGE,"E130.0"),sQuery(id+"F24.wireOp",EDGE,"E131.0"),sQuery(id+"F24.wireOp",EDGE,"E133"),sQuery(id+"F24.wireOp",EDGE,"E134"),sQuery(id+"F24.wireOp",EDGE,"E135.filletArc"),sQuery(id+"F24.wireOp",EDGE,"E136.0"),sQuery(id+"F24.wireOp",EDGE,"E137.filletArc")])],"isStart":true})]});
            var sketch = newSketch(context, id + "F26", { "sketchPlane" : qUnion([Q0])});
            skLineSegment(sketch, "E138", {"start": v(-1.5, 5.9) * mm, "end": v(27.96, 5.9) * mm, "construction": true});
            skCircle(sketch, "E139", {"center": v(25, 6.4) * mm, "radius": 3.5 * mm, "construction": true});
            skPoint(sketch, "E140", {"position": v(21.54, 5.9) * mm});
            skLineSegment(sketch, "E141", {"start": v(21.54, 10.8) * mm, "end": v(-1.5, 10.8) * mm, "construction": true});
            skPoint(sketch, "E142", {"position": v(10.02, 10.8) * mm});
            skLineSegment(sketch, "E143", {"start": v(10.02, 10.8) * mm, "end": v(10.02, 5.9) * mm, "construction": true});
            skCircle(sketch, "E144", {"center": v(10.02, 5.9) * mm, "radius": 1 * mm});
            skCircle(sketch, "E145", {"center": v(16.54, 5.9) * mm, "radius": 1 * mm});
            skCircle(sketch, "E146.MirrorC", {"center": v(3.5, 5.9) * mm, "radius": 1 * mm});
            skSolve(sketch);
        }
        {
            var Q0;
            Q0 = qSketchRegion(id + "F26", true);
            var Q1;
            {var subQ0=sQuery(id+"F6.wireOp",EDGE,"E55.filletArc");var subQ1=sQuery(id+"F6.wireOp",EDGE,"E52");var subQ2=sQuery(id+"F6.wireOp",EDGE,"E51");var subQ3=sQuery(id+"F6.wireOp",EDGE,"E50");var subQ4=sQuery(id+"F6.wireOp",EDGE,"E49.0");var subQ5=sQuery(id+"F6.wireOp",EDGE,"E48.0");var subQ6=sQuery(id+"F6.wireOp",EDGE,"E47.0");var subQ7=sQuery(id+"F6.wireOp",EDGE,"E46.0");var subQ8=sQuery(id+"F6.wireOp",EDGE,"E45.0");var subQ9=sQuery(id+"F6.wireOp",EDGE,"E44.0");var subQ10=sQuery(id+"F6.wireOp",EDGE,"E43.0");var subQ11=sQuery(id+"F6.wireOp",EDGE,"E42.0");var subQ12=sQuery(id+"F6.wireOp",EDGE,"E41.0");var subQ13=sQuery(id+"F6.wireOp",EDGE,"E40.0");var subQ14=sQuery(id+"F6.wireOp",EDGE,"E39.0");var subQ15=sQuery(id+"F6.wireOp",EDGE,"E38.0");Q1=makeQuery(id+"F25.boolean.opBoolean","MERGE",FACE,{"derivedFrom":[makeQuery(id+"F23.opPattern","COPY",FACE,{"derivedFrom":makeQuery(id+"F7.opExtrude","CAP_FACE",FACE,{"disambiguationData":[OSD([subQ15,subQ14,subQ13,subQ12,subQ11,subQ10,subQ9,subQ8,subQ7,subQ6,subQ5,subQ4,subQ3,subQ2,subQ1,subQ0])],"isStart":false}),"instanceName":"1"}),makeQuery(id+"F25.opExtrude","CAP_FACE",FACE,{"disambiguationData":[OSD([subQ15,subQ14,subQ13,subQ12,subQ11,subQ10,subQ9,subQ8,subQ7,subQ6,subQ5,subQ4,subQ3,subQ2,subQ1,subQ0]),OD(0.0)],"isStart":false}),makeQuery(id+"F25.opExtrude","CAP_FACE",FACE,{"disambiguationData":[OSD([subQ15,subQ14,subQ13,subQ12,subQ11,subQ10,subQ9,subQ8,subQ7,subQ6,subQ5,subQ4,subQ3,subQ2,subQ1,subQ0]),OD(1.0)],"isStart":false}),makeQuery(id+"F25.opExtrude","CAP_FACE",FACE,{"disambiguationData":[OSD([subQ15,subQ14,subQ13,subQ12,subQ11,subQ10,subQ9,subQ8,subQ7,subQ6,subQ5,subQ4,subQ3,subQ2,subQ1,subQ0]),OD(2.0)],"isStart":false})]});}
            extrude(context, id + "F27", {"entities" : qUnion([Q0]), "operationType" : NewBodyOperationType.REMOVE, "endBound" : BoundingType.UP_TO_SURFACE, "oppositeDirection" : true, "depth" : 25 * mm, "endBoundEntityFace" : qUnion([Q1]), "offsetDistance" : 25 * mm});
        }
        {
            var Q0;
            Q0=makeQuery(id+"F25.boolean.opBoolean","MERGE",FACE,{"derivedFrom":[makeQuery(id+"F23.opPattern","COPY",FACE,{"derivedFrom":makeQuery(id+"F7.opExtrude","CAP_FACE",FACE,{"disambiguationData":[OSD([sQuery(id+"F6.wireOp",EDGE,"E38.0"),sQuery(id+"F6.wireOp",EDGE,"E39.0"),sQuery(id+"F6.wireOp",EDGE,"E40.0"),sQuery(id+"F6.wireOp",EDGE,"E41.0"),sQuery(id+"F6.wireOp",EDGE,"E42.0"),sQuery(id+"F6.wireOp",EDGE,"E43.0"),sQuery(id+"F6.wireOp",EDGE,"E44.0"),sQuery(id+"F6.wireOp",EDGE,"E45.0"),sQuery(id+"F6.wireOp",EDGE,"E46.0"),sQuery(id+"F6.wireOp",EDGE,"E47.0"),sQuery(id+"F6.wireOp",EDGE,"E48.0"),sQuery(id+"F6.wireOp",EDGE,"E49.0"),sQuery(id+"F6.wireOp",EDGE,"E50"),sQuery(id+"F6.wireOp",EDGE,"E51"),sQuery(id+"F6.wireOp",EDGE,"E52"),sQuery(id+"F6.wireOp",EDGE,"E55.filletArc")])],"isStart":true}),"instanceName":"1"}),makeQuery(id+"F25.opExtrude","CAP_FACE",FACE,{"disambiguationData":[OSD([sQuery(id+"F24.wireOp",EDGE,"E119.0")])],"isStart":true}),makeQuery(id+"F25.opExtrude","CAP_FACE",FACE,{"disambiguationData":[OSD([sQuery(id+"F24.wireOp",EDGE,"E120.0"),sQuery(id+"F24.wireOp",EDGE,"E121.0"),sQuery(id+"F24.wireOp",EDGE,"E122.0"),sQuery(id+"F24.wireOp",EDGE,"E123.0"),sQuery(id+"F24.wireOp",EDGE,"E124.0"),sQuery(id+"F24.wireOp",EDGE,"E125.0")])],"isStart":true}),makeQuery(id+"F25.opExtrude","CAP_FACE",FACE,{"disambiguationData":[OSD([sQuery(id+"F24.wireOp",EDGE,"E127"),sQuery(id+"F24.wireOp",EDGE,"E128.0"),sQuery(id+"F24.wireOp",EDGE,"E130.0"),sQuery(id+"F24.wireOp",EDGE,"E131.0"),sQuery(id+"F24.wireOp",EDGE,"E133"),sQuery(id+"F24.wireOp",EDGE,"E134"),sQuery(id+"F24.wireOp",EDGE,"E135.filletArc"),sQuery(id+"F24.wireOp",EDGE,"E136.0"),sQuery(id+"F24.wireOp",EDGE,"E137.filletArc")])],"isStart":true})]});
            extrude(context, id + "F28", {"entities" : qUnion([Q0]), "operationType" : NewBodyOperationType.REMOVE, "oppositeDirection" : true, "depth" : 3.5 * mm, "offsetDistance" : 25 * mm});
        }
    });
